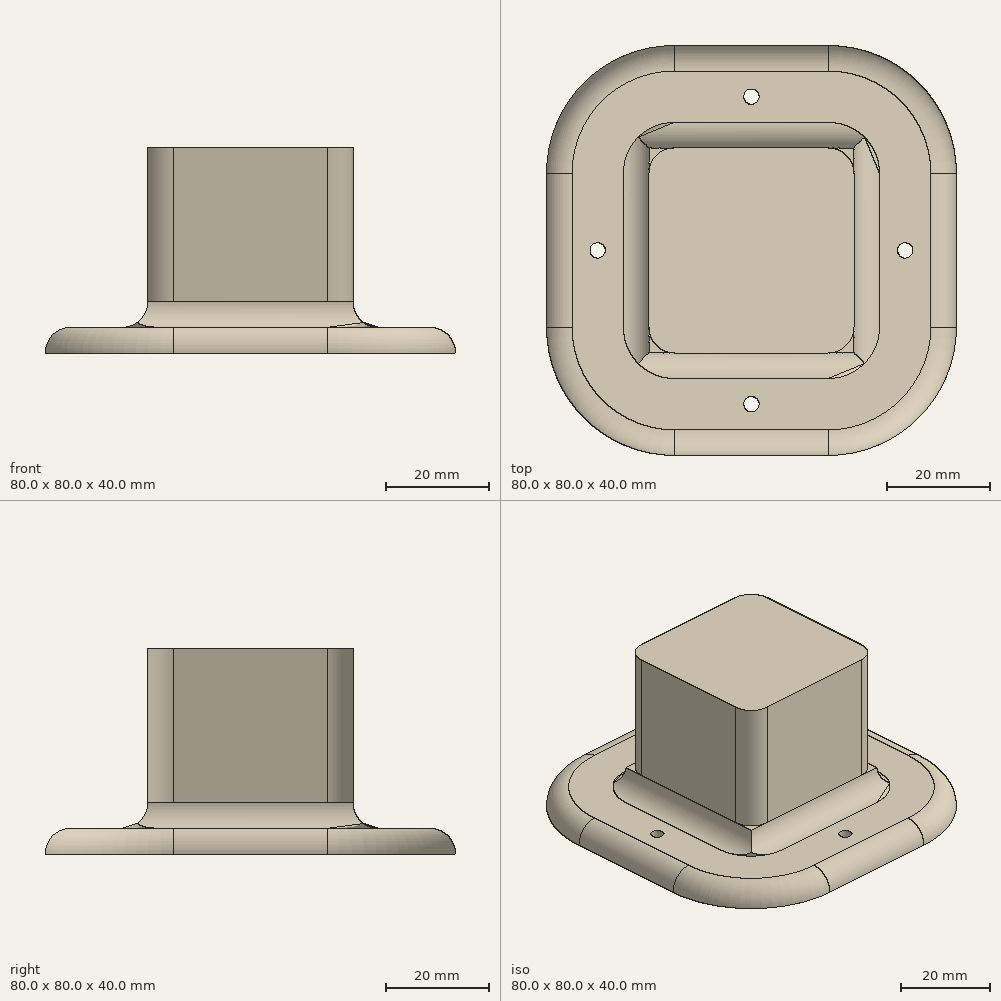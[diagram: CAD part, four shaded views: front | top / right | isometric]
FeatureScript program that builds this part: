
annotation { "Feature Type Name" : "Feature", "Feature Type Description" : "" }
export const myFeature = defineFeature(function(context is Context, id is Id, definition is map)
    precondition{}
    {
        {
            var Q0;
            Q0=qCreatedBy(makeId("Top.planeOp"),FACE);
            var sketch = newSketch(context, id + "F0", { "sketchPlane" : qUnion([Q0])});
            skLineSegment(sketch, "E0.bottom", {"start": v(5, 0) * mm, "end": v(35, 0) * mm});
            skLineSegment(sketch, "E0.top", {"start": v(5, 40) * mm, "end": v(35, 40) * mm});
            skLineSegment(sketch, "E0.left", {"start": v(0, 5) * mm, "end": v(0, 35) * mm});
            skLineSegment(sketch, "E0.right", {"start": v(40, 5) * mm, "end": v(40, 35) * mm});
            skLineSegment(sketch, "E1.bottom", {"start": v(5, -20) * mm, "end": v(35, -20) * mm});
            skLineSegment(sketch, "E1.top", {"start": v(5, 60) * mm, "end": v(35, 60) * mm});
            skLineSegment(sketch, "E1.left", {"start": v(-20, 5) * mm, "end": v(-20, 35) * mm});
            skLineSegment(sketch, "E1.right", {"start": v(60, 5) * mm, "end": v(60, 35) * mm});
            skPoint(sketch, "E2.visualSharp", {"position": v(0, 0) * mm});
            skArc(sketch, "E2.filletArc", {"start": v(0, 5) * mm, "mid": v(1.46, 1.46) * mm, "end": v(5, 0) * mm});
            skPoint(sketch, "E3.visualSharp", {"position": v(0, 40) * mm});
            skArc(sketch, "E3.filletArc", {"start": v(5, 40) * mm, "mid": v(1.46, 38.54) * mm, "end": v(0, 35) * mm});
            skPoint(sketch, "E4.visualSharp", {"position": v(40, 40) * mm});
            skArc(sketch, "E4.filletArc", {"start": v(40, 35) * mm, "mid": v(38.54, 38.54) * mm, "end": v(35, 40) * mm});
            skPoint(sketch, "E5.visualSharp", {"position": v(40, 0) * mm});
            skArc(sketch, "E5.filletArc", {"start": v(35, 0) * mm, "mid": v(38.54, 1.46) * mm, "end": v(40, 5) * mm});
            skPoint(sketch, "E6.visualSharp", {"position": v(-20, 60) * mm});
            skArc(sketch, "E6.filletArc", {"start": v(5, 60) * mm, "mid": v(-12.68, 52.68) * mm, "end": v(-20, 35) * mm});
            skPoint(sketch, "E7.visualSharp", {"position": v(60, 60) * mm});
            skArc(sketch, "E7.filletArc", {"start": v(60, 35) * mm, "mid": v(52.68, 52.68) * mm, "end": v(35, 60) * mm});
            skPoint(sketch, "E8.visualSharp", {"position": v(60, -20) * mm});
            skArc(sketch, "E8.filletArc", {"start": v(35, -20) * mm, "mid": v(52.68, -12.68) * mm, "end": v(60, 5) * mm});
            skPoint(sketch, "E9.visualSharp", {"position": v(-20, -20) * mm});
            skArc(sketch, "E9.filletArc", {"start": v(-20, 5) * mm, "mid": v(-12.68, -12.68) * mm, "end": v(5, -20) * mm});
            skLineSegment(sketch, "E10.bottom", {"start": v(5, 45) * mm, "end": v(35, 45) * mm});
            skLineSegment(sketch, "E10.top", {"start": v(5, -5) * mm, "end": v(35, -5) * mm});
            skLineSegment(sketch, "E10.left", {"start": v(-5, 35) * mm, "end": v(-5, 5) * mm});
            skLineSegment(sketch, "E10.right", {"start": v(45, 35) * mm, "end": v(45, 5) * mm});
            skPoint(sketch, "E11.visualSharp", {"position": v(-5, 45) * mm});
            skArc(sketch, "E11.filletArc", {"start": v(5, 45) * mm, "mid": v(-2.07, 42.07) * mm, "end": v(-5, 35) * mm});
            skPoint(sketch, "E12.visualSharp", {"position": v(45, 45) * mm});
            skArc(sketch, "E12.filletArc", {"start": v(45, 35) * mm, "mid": v(42.07, 42.07) * mm, "end": v(35, 45) * mm});
            skPoint(sketch, "E13.visualSharp", {"position": v(45, -5) * mm});
            skArc(sketch, "E13.filletArc", {"start": v(35, -5) * mm, "mid": v(42.07, -2.07) * mm, "end": v(45, 5) * mm});
            skPoint(sketch, "E14.visualSharp", {"position": v(-5, -5) * mm});
            skArc(sketch, "E14.filletArc", {"start": v(-5, 5) * mm, "mid": v(-2.07, -2.07) * mm, "end": v(5, -5) * mm});
            skLineSegment(sketch, "E15.bottom", {"start": v(-10, 50) * mm, "end": v(50, 50) * mm, "construction": true});
            skLineSegment(sketch, "E15.top", {"start": v(-10, -10) * mm, "end": v(50, -10) * mm, "construction": true});
            skLineSegment(sketch, "E15.left", {"start": v(-10, 50) * mm, "end": v(-10, -10) * mm, "construction": true});
            skLineSegment(sketch, "E15.right", {"start": v(50, 50) * mm, "end": v(50, -10) * mm, "construction": true});
            skLineSegment(sketch, "E16", {"start": v(20, 50) * mm, "end": v(20, -10) * mm, "construction": true});
            skLineSegment(sketch, "E17", {"start": v(-10, 20) * mm, "end": v(50, 20) * mm, "construction": true});
            skCircle(sketch, "E18", {"center": v(20, -10) * mm, "radius": 1.5 * mm});
            skCircle(sketch, "E19", {"center": v(-10, 20) * mm, "radius": 1.5 * mm});
            skCircle(sketch, "E20", {"center": v(50, 20) * mm, "radius": 1.5 * mm});
            skCircle(sketch, "E21", {"center": v(20, 50) * mm, "radius": 1.5 * mm});
            skSolve(sketch);
        }
        {
            var Q0;
            Q0=makeQuery(id+"F0.imprint","IMPRINT",FACE,{"disambiguationData":[TD([[makeQuery(id+"F0.imprint","IMPRINT",EDGE,{"derivedFrom":sQuery(id+"F0.wireOp",EDGE,"E0.bottom")}),1.0]])]});
            extrude(context, id + "F1", {"entities" : qUnion([Q0]), "depth" : 40 * mm});
        }
        {
            var Q0;
            Q0=makeQuery(id+"F0.imprint","IMPRINT",FACE,{"disambiguationData":[TD([[makeQuery(id+"F0.imprint","IMPRINT",EDGE,{"derivedFrom":sQuery(id+"F0.wireOp",EDGE,"E1.bottom")}),1.0]])]});
            var Q1;
            Q1=makeQuery(id+"F0.imprint","IMPRINT",FACE,{"disambiguationData":[TD([[makeQuery(id+"F0.imprint","IMPRINT",EDGE,{"derivedFrom":sQuery(id+"F0.wireOp",EDGE,"E0.bottom")}),-1.0]])]});
            extrude(context, id + "F2", {"entities" : qUnion([Q0, Q1]), "operationType" : NewBodyOperationType.ADD, "depth" : 5 * mm});
        }
        {
            var Q0;
            Q0=makeQuery(id+"F2.opExtrude","CAP_EDGE",EDGE,{"disambiguationData":[OSD([sQuery(id+"F0.wireOp",EDGE,"E1.bottom")])],"isStart":false});
            var Q1;
            Q1=makeQuery(id+"F1.opExtrude","SWEPT_EDGE",EDGE,{"disambiguationData":[OSD([sQuery(id+"F0.wireOp",EDGE,"E0.left"),sQuery(id+"F0.wireOp",EDGE,"E2.filletArc")])]});
            fillet(context, id + "F3", {"entities" : qUnion([Q0, Q1]), "radius" : 5 * mm, "tangentPropagation" : true, "allowEdgeOverflow" : false});
        }
        {
            var Q0;
            Q0=makeQuery(id+"F0.imprint","IMPRINT",FACE,{"disambiguationData":[TD([[makeQuery(id+"F0.imprint","IMPRINT",EDGE,{"derivedFrom":sQuery(id+"F0.wireOp",EDGE,"E0.bottom")}),-1.0]])]});
            extrude(context, id + "F4", {"entities" : qUnion([Q0]), "operationType" : NewBodyOperationType.ADD, "depth" : 10 * mm});
        }
        {
            var Q0;
            Q0=makeQuery(id+"F4.opExtrude","SWEPT_FACE",FACE,{"disambiguationData":[OSD([sQuery(id+"F0.wireOp",EDGE,"E10.top")])]});
            var sketch = newSketch(context, id + "F5", { "sketchPlane" : qUnion([Q0])});
            skLineSegment(sketch, "E22", {"start": v(-32.24, 10) * mm, "end": v(65.05, 10) * mm, "construction": true});
            skLineSegment(sketch, "E23", {"start": v(-5, 26.24) * mm, "end": v(-5, -9.22) * mm, "construction": true});
            skLineSegment(sketch, "E24", {"start": v(45, 27.8) * mm, "end": v(45, -11.2) * mm, "construction": true});
            skLineSegment(sketch, "E25", {"start": v(-32.65, 5) * mm, "end": v(69.34, 5) * mm});
            skCircle(sketch, "E26", {"center": v(-5, 10) * mm, "radius": 5 * mm});
            skCircle(sketch, "E27", {"center": v(45, 10) * mm, "radius": 5 * mm});
            skSolve(sketch);
        }
        {
            var Q0;
            Q0 = qSketchRegion(id + "F5", true);
            extrude(context, id + "F6", {"entities" : qUnion([Q0]), "operationType" : NewBodyOperationType.REMOVE, "oppositeDirection" : true, "depth" : 50 * mm});
        }
        {
            var Q0;
            Q0 = qSketchRegion(id + "F5", true);
            extrude(context, id + "F7", {"entities" : qUnion([Q0]), "operationType" : NewBodyOperationType.REMOVE, "depth" : 5 * mm});
        }
        {
            var Q0;
            Q0=makeQuery(id+"F1.opExtrude","SWEPT_FACE",FACE,{"disambiguationData":[OSD([sQuery(id+"F0.wireOp",EDGE,"E0.right")])]});
            var sketch = newSketch(context, id + "F8", { "sketchPlane" : qUnion([Q0])});
            skLineSegment(sketch, "E28", {"start": v(-5, 43.77) * mm, "end": v(-5, -14.46) * mm, "construction": true});
            skLineSegment(sketch, "E29", {"start": v(45, 42.09) * mm, "end": v(45, -15.54) * mm, "construction": true});
            skLineSegment(sketch, "E30", {"start": v(63.88, 10) * mm, "end": v(-27.96, 10) * mm, "construction": true});
            skLineSegment(sketch, "E31", {"start": v(-27.6, 5) * mm, "end": v(66.52, 5) * mm, "construction": true});
            skCircle(sketch, "E32", {"center": v(-5, 10) * mm, "radius": 5 * mm});
            skCircle(sketch, "E33", {"center": v(45, 10) * mm, "radius": 5 * mm});
            skLineSegment(sketch, "E34", {"start": v(0, 56.55) * mm, "end": v(0, -23.36) * mm, "construction": true});
            skLineSegment(sketch, "E35", {"start": v(40, 61.16) * mm, "end": v(40, -31.48) * mm, "construction": true});
            skSolve(sketch);
        }
        {
            var Q0;
            Q0 = qSketchRegion(id + "F8", true);
            extrude(context, id + "F9", {"entities" : qUnion([Q0]), "operationType" : NewBodyOperationType.REMOVE, "oppositeDirection" : true, "depth" : 50 * mm});
        }
        {
            var Q0;
            Q0 = qSketchRegion(id + "F8", true);
            extrude(context, id + "F10", {"entities" : qUnion([Q0]), "operationType" : NewBodyOperationType.REMOVE, "depth" : 5 * mm});
        }
    });
